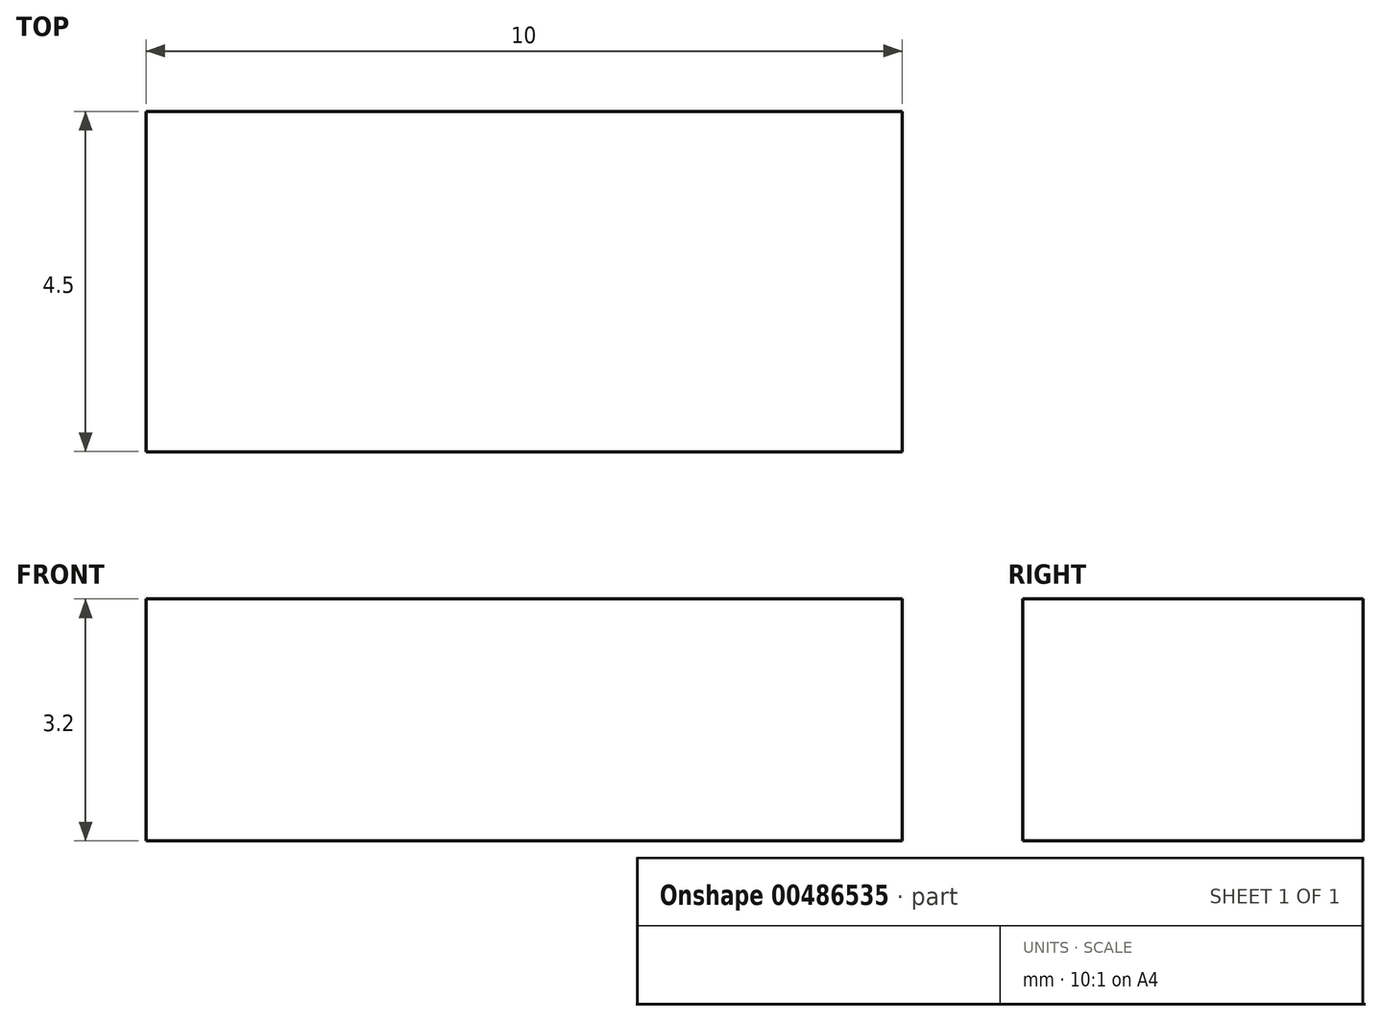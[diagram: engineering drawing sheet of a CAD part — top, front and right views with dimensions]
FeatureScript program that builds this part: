
annotation { "Feature Type Name" : "Feature", "Feature Type Description" : "" }
export const myFeature = defineFeature(function(context is Context, id is Id, definition is map)
    precondition{}
    {
        {
            var Q0;
            Q0=qCreatedBy(makeId("Top.planeOp"),FACE);
            var sketch = newSketch(context, id + "F0", { "sketchPlane" : qUnion([Q0])});
            skLineSegment(sketch, "E0.bottom", {"start": v(-20.63, 15.08) * mm, "end": v(-30.63, 15.08) * mm});
            skLineSegment(sketch, "E0.top", {"start": v(-20.63, 19.58) * mm, "end": v(-30.63, 19.58) * mm});
            skLineSegment(sketch, "E0.left", {"start": v(-20.63, 15.08) * mm, "end": v(-20.63, 19.58) * mm});
            skLineSegment(sketch, "E0.right", {"start": v(-30.63, 15.08) * mm, "end": v(-30.63, 19.58) * mm});
            skPoint(sketch, "E0.middle", {"position": v(-25.63, 17.33) * mm});
            skSolve(sketch);
        }
        {
            var Q0;
            Q0 = qSketchRegion(id + "F0", true);
            extrude(context, id + "F1", {"entities" : qUnion([Q0]), "depth" : 3.2 * mm, "offsetDistance" : 25 * mm});
        }
    });
